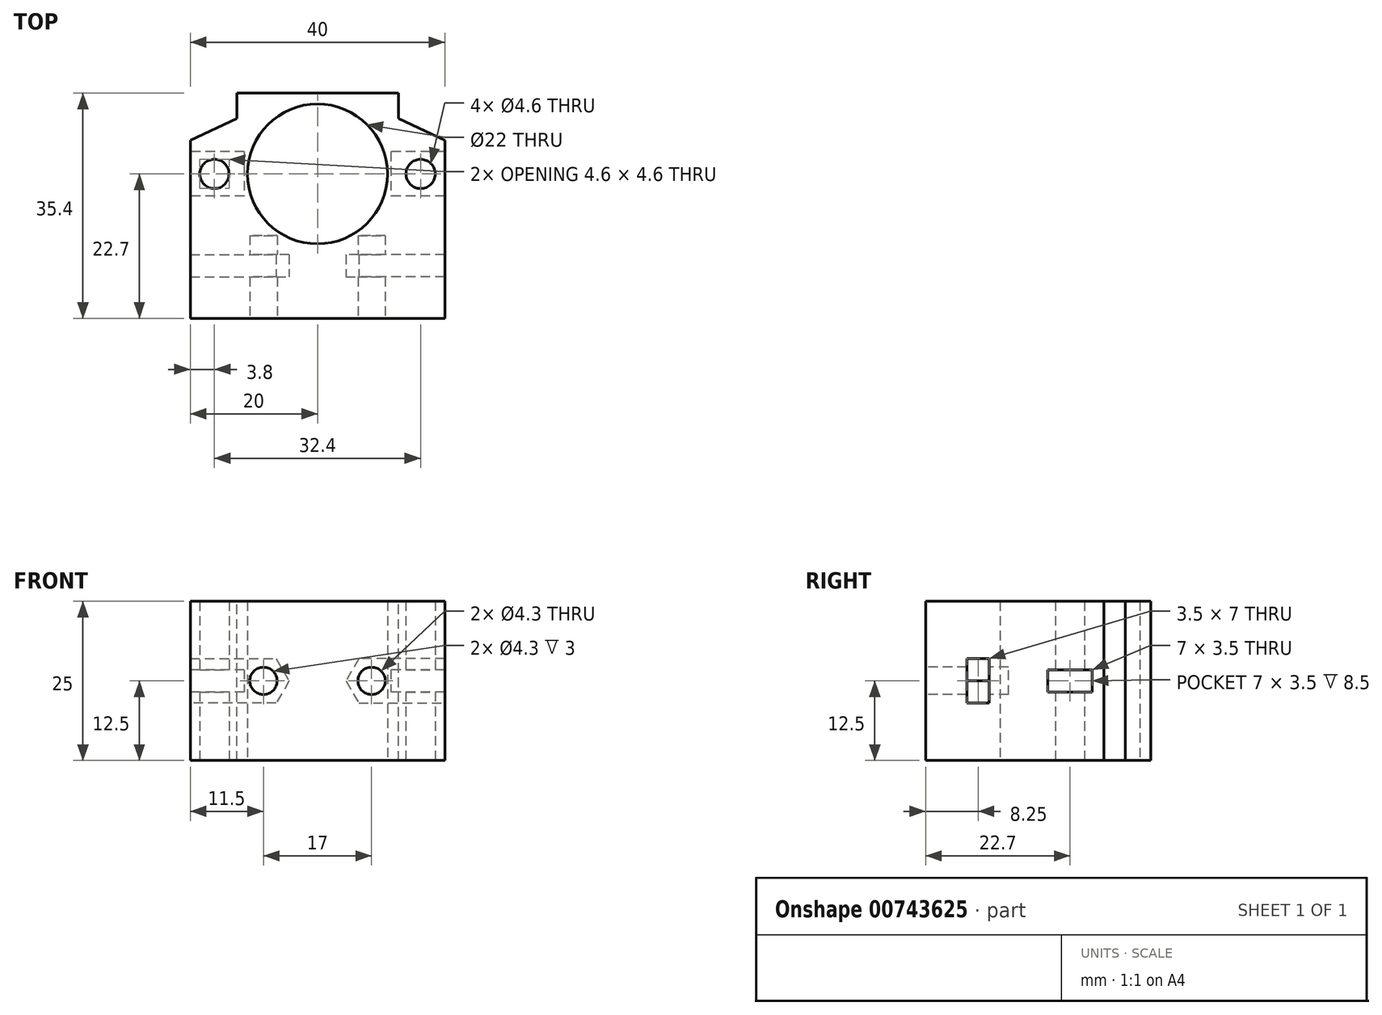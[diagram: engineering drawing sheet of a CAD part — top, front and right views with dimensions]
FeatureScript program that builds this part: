
annotation { "Feature Type Name" : "Feature", "Feature Type Description" : "" }
export const myFeature = defineFeature(function(context is Context, id is Id, definition is map)
    precondition{}
    {
        {
            var Q0;
            Q0=qCreatedBy(makeId("Top.planeOp"),FACE);
            var sketch = newSketch(context, id + "F0", { "sketchPlane" : qUnion([Q0])});
            skCircle(sketch, "E0", {"center": v(0, 0) * mm, "radius": 11 * mm});
            skCircle(sketch, "E1", {"center": v(-16.2, 0) * mm, "radius": 2.3 * mm});
            skCircle(sketch, "E2", {"center": v(16.2, 0) * mm, "radius": 2.3 * mm});
            skLineSegment(sketch, "E3.bottom", {"start": v(-20, 12.7) * mm, "end": v(20, 12.7) * mm});
            skLineSegment(sketch, "E3.top", {"start": v(-20, -22.7) * mm, "end": v(20, -22.7) * mm});
            skLineSegment(sketch, "E3.left", {"start": v(-20, 12.7) * mm, "end": v(-20, -22.7) * mm});
            skLineSegment(sketch, "E3.right", {"start": v(20, 12.7) * mm, "end": v(20, -22.7) * mm});
            skSolve(sketch);
        }
        {
            var Q0;
            Q0 = qSketchRegion(id + "F0", true);
            extrude(context, id + "F1", {"entities" : qUnion([Q0]), "depth" : 25 * mm, "offsetDistance" : 25 * mm});
        }
        {
            var Q0;
            Q0=makeQuery(id+"F1.opExtrude","SWEPT_FACE",FACE,{"disambiguationData":[OSD([sQuery(id+"F0.wireOp",EDGE,"E3.top")])]});
            var sketch = newSketch(context, id + "F2", { "sketchPlane" : qUnion([Q0])});
            skCircle(sketch, "E4", {"center": v(-8.5, 12.5) * mm, "radius": 2.15 * mm});
            skCircle(sketch, "E5.MirrorC", {"center": v(8.5, 12.5) * mm, "radius": 2.15 * mm});
            skSolve(sketch);
        }
        {
            var Q0;
            Q0 = qSketchRegion(id + "F2", true);
            extrude(context, id + "F3", {"entities" : qUnion([Q0]), "operationType" : NewBodyOperationType.REMOVE, "oppositeDirection" : true, "depth" : 13 * mm, "offsetDistance" : 25 * mm});
        }
        {
            var Q0;
            Q0=makeQuery(id+"F1.opExtrude","SWEPT_FACE",FACE,{"disambiguationData":[OSD([sQuery(id+"F0.wireOp",EDGE,"E3.top")])]});
            var sketch = newSketch(context, id + "F4", { "sketchPlane" : qUnion([Q0])});
            skCircle(sketch, "E6.cCircle", {"center": v(-8.5, 12.5) * mm, "radius": 3.5 * mm, "construction": true});
            skLineSegment(sketch, "E6.0", {"start": v(-10.52, 16) * mm, "end": v(-6.48, 16) * mm});
            skLineSegment(sketch, "E6.1", {"start": v(-6.48, 16) * mm, "end": v(-4.46, 12.5) * mm});
            skLineSegment(sketch, "E6.2", {"start": v(-4.46, 12.5) * mm, "end": v(-6.48, 9) * mm});
            skLineSegment(sketch, "E6.3", {"start": v(-6.48, 9) * mm, "end": v(-10.52, 9) * mm});
            skLineSegment(sketch, "E6.4", {"start": v(-10.52, 9) * mm, "end": v(-12.54, 12.5) * mm});
            skLineSegment(sketch, "E6.5", {"start": v(-12.54, 12.5) * mm, "end": v(-10.52, 16) * mm});
            skPoint(sketch, "E6.0.midPoint", {"position": v(-8.5, 16) * mm});
            skLineSegment(sketch, "E7.MirrorCS", {"start": v(10.52, 16) * mm, "end": v(6.48, 16) * mm});
            skLineSegment(sketch, "E8.MirrorCS", {"start": v(6.48, 9) * mm, "end": v(10.52, 9) * mm});
            skLineSegment(sketch, "E9.MirrorCS", {"start": v(12.54, 12.5) * mm, "end": v(10.52, 16) * mm});
            skPoint(sketch, "E10.MirrorP", {"position": v(8.5, 16) * mm});
            skCircle(sketch, "E11.MirrorC", {"center": v(8.5, 12.5) * mm, "radius": 3.5 * mm, "construction": true});
            skLineSegment(sketch, "E12.MirrorCS", {"start": v(6.48, 16) * mm, "end": v(4.46, 12.5) * mm});
            skLineSegment(sketch, "E13.MirrorCS", {"start": v(4.46, 12.5) * mm, "end": v(6.48, 9) * mm});
            skLineSegment(sketch, "E14.MirrorCS", {"start": v(10.52, 9) * mm, "end": v(12.54, 12.5) * mm});
            skSolve(sketch);
        }
        {
            var Q0;
            Q0 = qSketchRegion(id + "F4", true);
            extrude(context, id + "F5", {"entities" : qUnion([Q0]), "operationType" : NewBodyOperationType.REMOVE, "oppositeDirection" : true, "depth" : 10 * mm, "offsetDistance" : 25 * mm, "hasSecondDirection" : true, "secondDirectionOppositeDirection" : true, "secondDirectionDepth" : 6.5 * mm});
        }
        {
            var Q0;
            Q0=makeQuery(id+"F1.opExtrude","SWEPT_FACE",FACE,{"disambiguationData":[OSD([sQuery(id+"F0.wireOp",EDGE,"E3.left")])]});
            var sketch = newSketch(context, id + "F6", { "sketchPlane" : qUnion([Q0])});
            skLineSegment(sketch, "E15.bottom", {"start": v(16.2, 16) * mm, "end": v(12.7, 16) * mm});
            skLineSegment(sketch, "E15.top", {"start": v(16.2, 9) * mm, "end": v(12.7, 9) * mm});
            skLineSegment(sketch, "E15.left", {"start": v(16.2, 16) * mm, "end": v(16.2, 9) * mm});
            skLineSegment(sketch, "E15.right", {"start": v(12.7, 16) * mm, "end": v(12.7, 9) * mm});
            skSolve(sketch);
        }
        {
            var Q0;
            Q0 = qSketchRegion(id + "F6", true);
            extrude(context, id + "F7", {"entities" : qUnion([Q0]), "operationType" : NewBodyOperationType.REMOVE, "oppositeDirection" : true, "depth" : 10 * mm, "offsetDistance" : 25 * mm});
        }
        {
            var Q0;
            Q0 = qSketchRegion(id + "F6", true);
            extrude(context, id + "F8", {"entities" : qUnion([Q0]), "operationType" : NewBodyOperationType.REMOVE, "oppositeDirection" : true, "depth" : 50 * mm, "offsetDistance" : 25 * mm, "hasSecondDirection" : true, "secondDirectionOppositeDirection" : true, "secondDirectionDepth" : 27 * mm});
        }
        {
            var Q0;
            Q0=makeQuery(id+"F1.opExtrude","CAP_FACE",FACE,{"disambiguationData":[OSD([sQuery(id+"F0.wireOp",EDGE,"E0"),sQuery(id+"F0.wireOp",EDGE,"E1"),sQuery(id+"F0.wireOp",EDGE,"E2"),sQuery(id+"F0.wireOp",EDGE,"E3.bottom"),sQuery(id+"F0.wireOp",EDGE,"E3.top"),sQuery(id+"F0.wireOp",EDGE,"E3.left"),sQuery(id+"F0.wireOp",EDGE,"E3.right")])],"isStart":false});
            var sketch = newSketch(context, id + "F9", { "sketchPlane" : qUnion([Q0])});
            skLineSegment(sketch, "E16", {"start": v(-12.7, 8.7) * mm, "end": v(-12.7, 12.7) * mm});
            skLineSegment(sketch, "E17", {"start": v(-12.7, 8.7) * mm, "end": v(-20, 5.3) * mm});
            skLineSegment(sketch, "E18.MirrorCS", {"start": v(12.7, 8.7) * mm, "end": v(20, 5.3) * mm});
            skLineSegment(sketch, "E19.MirrorCS", {"start": v(12.7, 8.7) * mm, "end": v(12.7, 12.7) * mm});
            skSolve(sketch);
        }
        {
            var Q0;
            Q0=makeQuery(id+"F1.opExtrude","SWEPT_FACE",FACE,{"disambiguationData":[OSD([sQuery(id+"F0.wireOp",EDGE,"E3.left")])]});
            var sketch = newSketch(context, id + "F10", { "sketchPlane" : qUnion([Q0])});
            skLineSegment(sketch, "E20.bottom", {"start": v(-3.5, 14.25) * mm, "end": v(3.5, 14.25) * mm});
            skLineSegment(sketch, "E20.top", {"start": v(-3.5, 10.75) * mm, "end": v(3.5, 10.75) * mm});
            skLineSegment(sketch, "E20.left", {"start": v(-3.5, 14.25) * mm, "end": v(-3.5, 10.75) * mm});
            skLineSegment(sketch, "E20.right", {"start": v(3.5, 14.25) * mm, "end": v(3.5, 10.75) * mm});
            skPoint(sketch, "E20.middle", {"position": v(0, 12.5) * mm});
            skSolve(sketch);
        }
        {
            var Q0;
            Q0 = qSketchRegion(id + "F10", true);
            extrude(context, id + "F11", {"entities" : qUnion([Q0]), "operationType" : NewBodyOperationType.REMOVE, "oppositeDirection" : true, "depth" : 8.5 * mm, "offsetDistance" : 25 * mm});
        }
        {
            var Q0;
            Q0 = qSketchRegion(id + "F10", true);
            extrude(context, id + "F12", {"entities" : qUnion([Q0]), "operationType" : NewBodyOperationType.REMOVE, "oppositeDirection" : true, "depth" : 50 * mm, "offsetDistance" : 25 * mm, "hasSecondDirection" : true, "secondDirectionOppositeDirection" : true, "secondDirectionDepth" : 31.5 * mm});
        }
        {
            var Q0;
            {var subQ0=sQuery(id+"F9.wireOp",EDGE,"E16");Q0=makeQuery(id+"F9.imprint","IMPRINT",FACE,{"disambiguationData":[TD([[makeQuery(id+"F9.imprint","IMPRINT",EDGE,{"derivedFrom":subQ0}),1.0]])]});}
            var Q1;
            {var subQ0=sQuery(id+"F9.wireOp",EDGE,"E18.MirrorCS");Q1=makeQuery(id+"F9.imprint","IMPRINT",FACE,{"disambiguationData":[TD([[makeQuery(id+"F9.imprint","IMPRINT",EDGE,{"derivedFrom":subQ0}),1.0]])]});}
            extrude(context, id + "F13", {"entities" : qUnion([Q0, Q1]), "operationType" : NewBodyOperationType.REMOVE, "oppositeDirection" : true, "depth" : 25 * mm, "offsetDistance" : 25 * mm});
        }
    });
